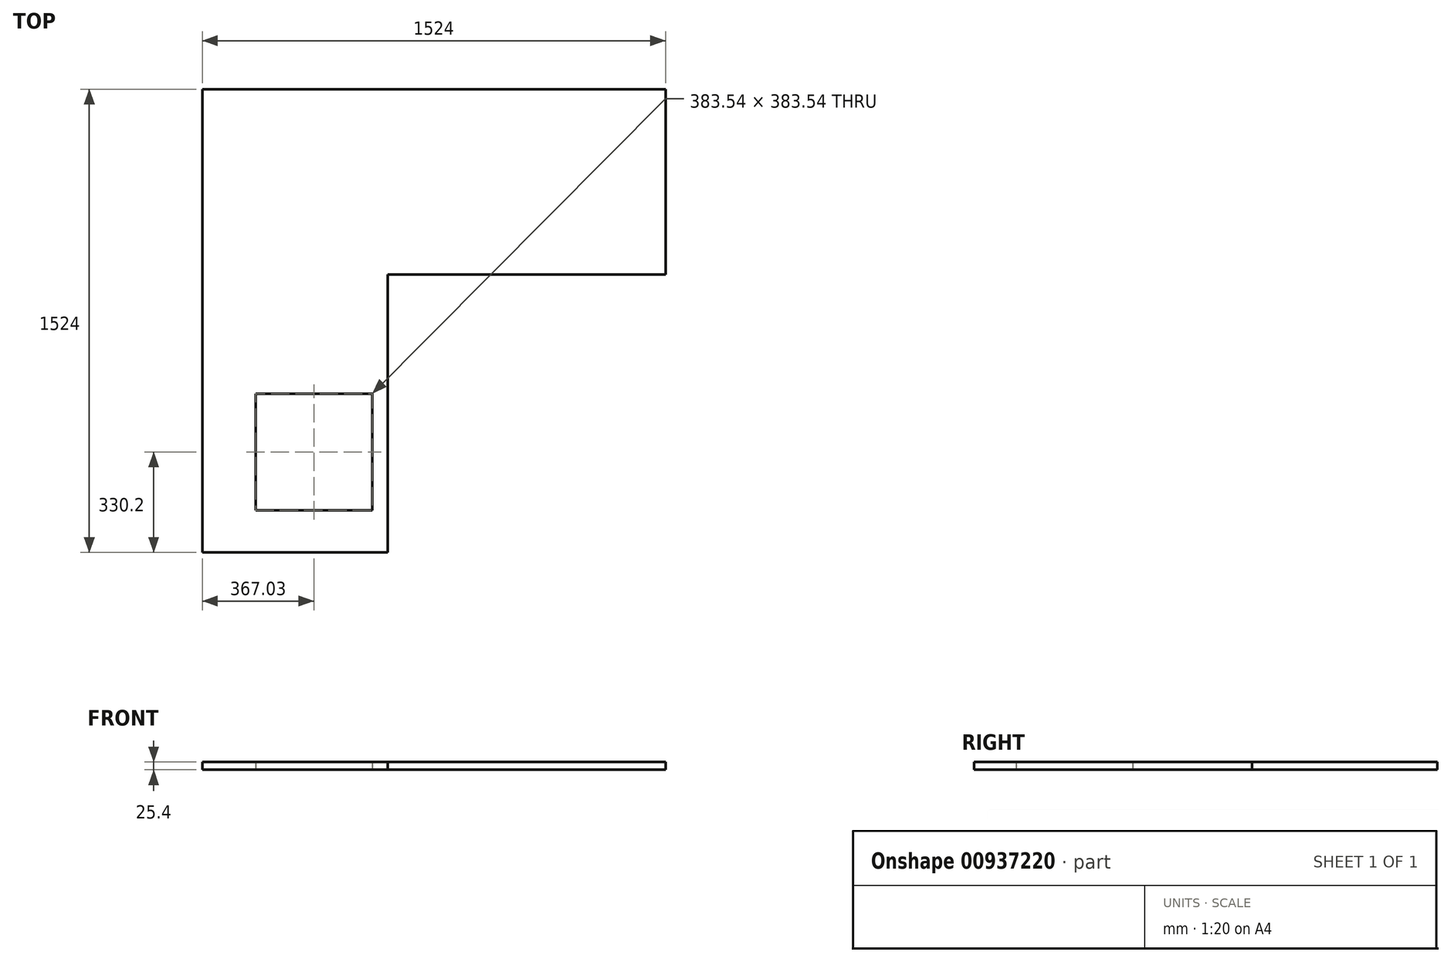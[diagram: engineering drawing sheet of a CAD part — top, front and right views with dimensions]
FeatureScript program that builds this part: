
annotation { "Feature Type Name" : "Feature", "Feature Type Description" : "" }
export const myFeature = defineFeature(function(context is Context, id is Id, definition is map)
    precondition{}
    {
        {
            var Q0;
            Q0=qCreatedBy(makeId("Top.planeOp"),FACE);
            var sketch = newSketch(context, id + "F0", { "sketchPlane" : qUnion([Q0])});
            skLineSegment(sketch, "E0.bottom", {"start": v(-50.8, -392.43) * mm, "end": v(-434.34, -392.43) * mm});
            skLineSegment(sketch, "E0.top", {"start": v(-50.8, -775.97) * mm, "end": v(-434.34, -775.97) * mm});
            skLineSegment(sketch, "E0.left", {"start": v(-50.8, -392.43) * mm, "end": v(-50.8, -775.97) * mm});
            skLineSegment(sketch, "E0.right", {"start": v(-434.34, -392.43) * mm, "end": v(-434.34, -775.97) * mm});
            skPoint(sketch, "E0.middle", {"position": v(-242.57, -584.2) * mm});
            skSolve(sketch);
        }
        {
            var Q0;
            Q0=makeQuery(id+"F0.imprint","IMPRINT",FACE,{"disambiguationData":[TD([[makeQuery(id+"F0.imprint","IMPRINT",EDGE,{"derivedFrom":sQuery(id+"F0.wireOp",EDGE,"E0.bottom")}),1.0]])]});
            var sketch = newSketch(context, id + "F1", { "sketchPlane" : qUnion([Q0])});
            skLineSegment(sketch, "E1", {"start": v(-609.6, 609.6) * mm, "end": v(914.4, 609.6) * mm});
            skLineSegment(sketch, "E2", {"start": v(914.4, 609.6) * mm, "end": v(914.4, 0) * mm});
            skLineSegment(sketch, "E3", {"start": v(914.4, 0) * mm, "end": v(0, 0) * mm});
            skLineSegment(sketch, "E4", {"start": v(0, 0) * mm, "end": v(0, -914.4) * mm});
            skLineSegment(sketch, "E5", {"start": v(0, -914.4) * mm, "end": v(-609.6, -914.4) * mm});
            skLineSegment(sketch, "E6", {"start": v(-609.6, -914.4) * mm, "end": v(-609.6, 609.6) * mm});
            skSolve(sketch);
        }
        {
            var Q0;
            Q0=makeQuery(id+"F1.imprint","IMPRINT",FACE,{"disambiguationData":[TD([[makeQuery(id+"F1.imprint","IMPRINT",EDGE,{"derivedFrom":sQuery(id+"F1.wireOp",EDGE,"E1")}),-1.0]])]});
            extrude(context, id + "F2", {"entities" : qUnion([Q0]), "depth" : 25.4 * mm, "offsetDistance" : 25.4 * mm});
        }
    });
